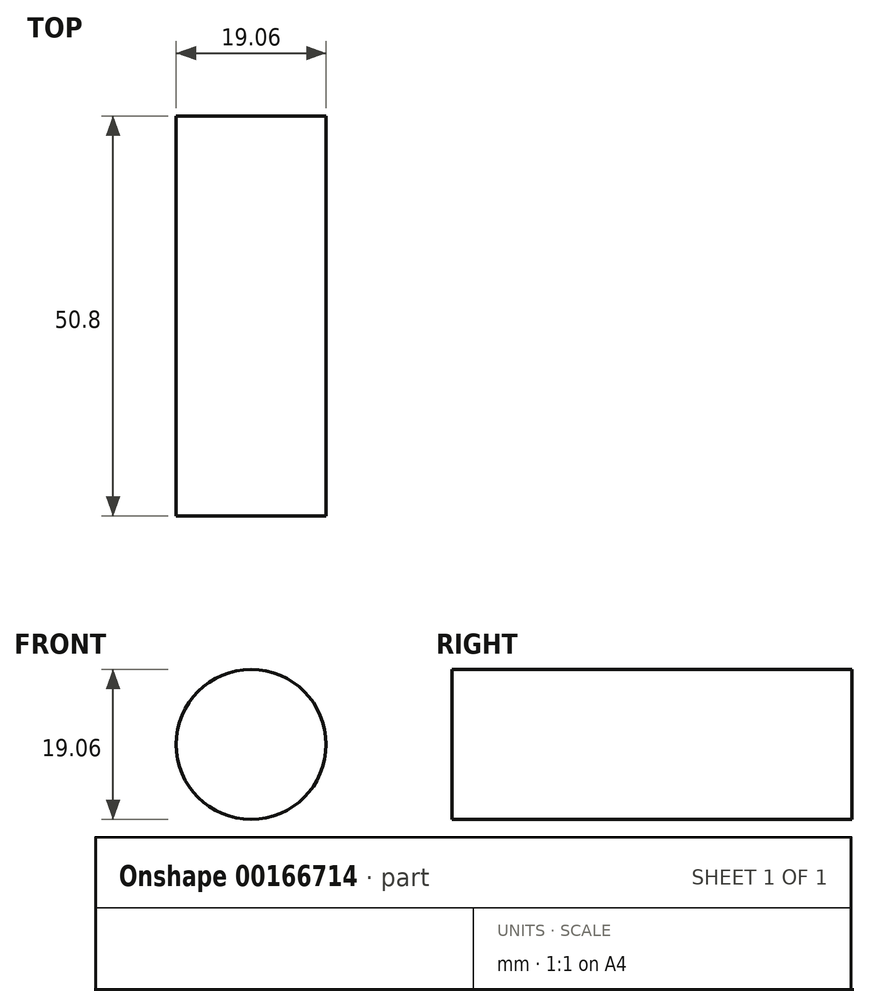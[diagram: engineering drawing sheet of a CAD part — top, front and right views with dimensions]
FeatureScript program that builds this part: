
annotation { "Feature Type Name" : "Feature", "Feature Type Description" : "" }
export const myFeature = defineFeature(function(context is Context, id is Id, definition is map)
    precondition{}
    {
        {
            var Q0;
            Q0=qCreatedBy(makeId("Front.planeOp"),FACE);
            var sketch = newSketch(context, id + "F0", { "sketchPlane" : qUnion([Q0])});
            skCircle(sketch, "E0", {"center": v(0, 0) * mm, "radius": 9.53 * mm});
            skSolve(sketch);
        }
        {
            var Q0;
            Q0 = qSketchRegion(id + "F0", true);
            extrude(context, id + "F1", {"entities" : qUnion([Q0]), "depth" : 25.4 * mm});
        }
        {
            var Q0;
            Q0=makeQuery(id+"F1.opExtrude","CAP_FACE",FACE,{"disambiguationData":[OSD([sQuery(id+"F0.wireOp",EDGE,"E0")])],"isStart":false});
            extrude(context, id + "F2", {"entities" : qUnion([Q0]), "operationType" : NewBodyOperationType.ADD, "depth" : 25.4 * mm});
        }
    });
